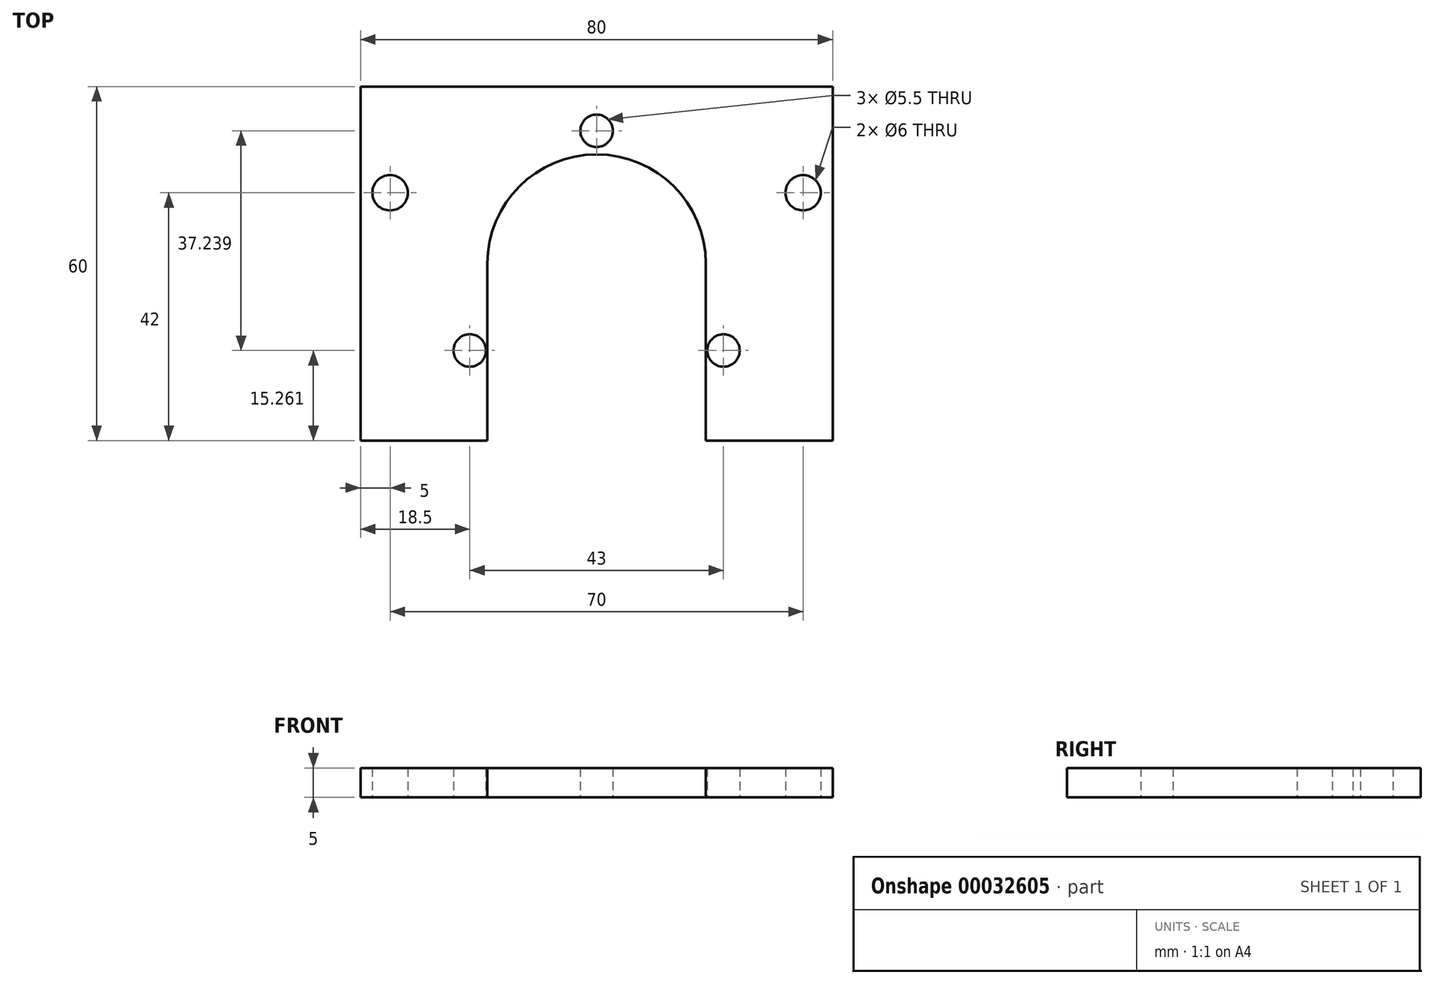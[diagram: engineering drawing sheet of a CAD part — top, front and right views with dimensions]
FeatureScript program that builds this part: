
annotation { "Feature Type Name" : "Feature", "Feature Type Description" : "" }
export const myFeature = defineFeature(function(context is Context, id is Id, definition is map)
    precondition{}
    {
        {
            var Q0;
            Q0=qCreatedBy(makeId("Top.planeOp"),FACE);
            var sketch = newSketch(context, id + "F0", { "sketchPlane" : qUnion([Q0])});
            skLineSegment(sketch, "E0.bottom", {"start": v(-40, -30) * mm, "end": v(40, -30) * mm});
            skLineSegment(sketch, "E0.top", {"start": v(-40, 30) * mm, "end": v(40, 30) * mm});
            skLineSegment(sketch, "E0.left", {"start": v(-40, -30) * mm, "end": v(-40, 30) * mm});
            skLineSegment(sketch, "E0.right", {"start": v(40, -30) * mm, "end": v(40, 30) * mm});
            skPoint(sketch, "E0.middle", {"position": v(0, 0) * mm});
            skCircle(sketch, "E1", {"center": v(0, 0) * mm, "radius": 18.5 * mm});
            skLineSegment(sketch, "E2", {"start": v(-18.5, 0) * mm, "end": v(-18.5, -30) * mm});
            skLineSegment(sketch, "E3", {"start": v(18.5, 0) * mm, "end": v(18.5, -30) * mm});
            skCircle(sketch, "E4", {"center": v(0, 22.5) * mm, "radius": 2.75 * mm});
            skCircle(sketch, "E5", {"center": v(-21.5, -14.74) * mm, "radius": 2.75 * mm});
            skCircle(sketch, "E6", {"center": v(21.5, -14.74) * mm, "radius": 2.75 * mm});
            skCircle(sketch, "E7", {"center": v(35, 12) * mm, "radius": 3 * mm});
            skCircle(sketch, "E8", {"center": v(-35, 12) * mm, "radius": 3 * mm});
            skSolve(sketch);
        }
        {
            var Q0;
            Q0=makeQuery(id+"F0.imprint","IMPRINT",FACE,{"disambiguationData":[TD([[makeQuery(id+"F0.imprint","IMPRINT",EDGE,{"derivedFrom":sQuery(id+"F0.wireOp",EDGE,"E0.top")}),-1.0]])]});
            extrude(context, id + "F1", {"entities" : qUnion([Q0]), "depth" : 5 * mm});
        }
    });
